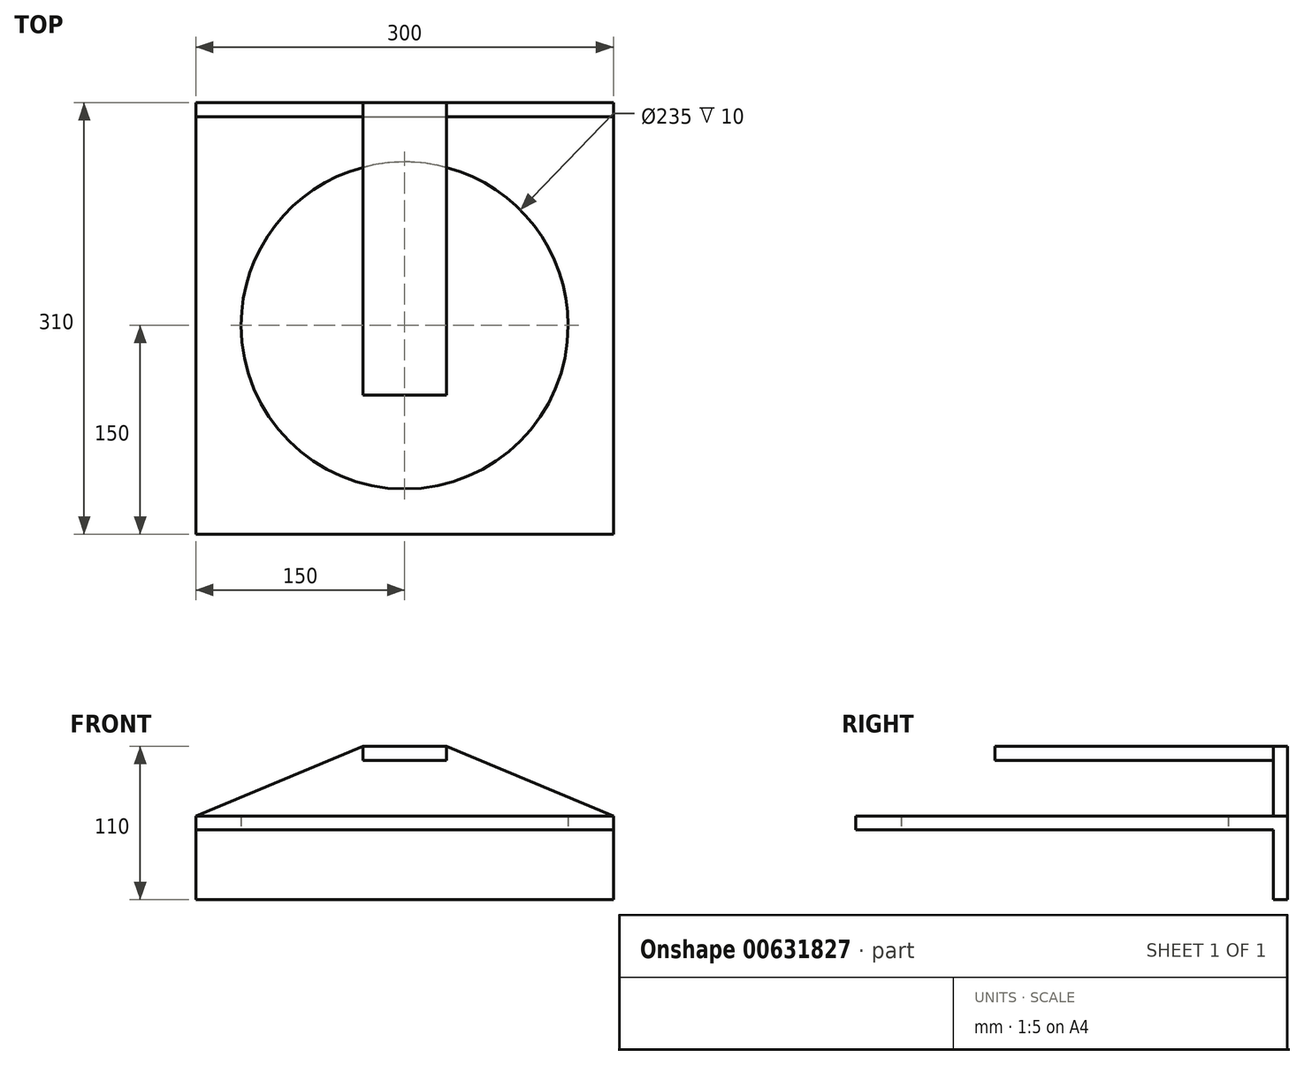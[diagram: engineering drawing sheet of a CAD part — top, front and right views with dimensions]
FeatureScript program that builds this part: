
annotation { "Feature Type Name" : "Feature", "Feature Type Description" : "" }
export const myFeature = defineFeature(function(context is Context, id is Id, definition is map)
    precondition{}
    {
        {
            var Q0;
            Q0=qCreatedBy(makeId("Front.planeOp"),FACE);
            var sketch = newSketch(context, id + "F0", { "sketchPlane" : qUnion([Q0])});
            skLineSegment(sketch, "E0.bottom", {"start": v(150, -30) * mm, "end": v(-150, -30) * mm});
            skLineSegment(sketch, "E0.top", {"start": v(150, 30) * mm, "end": v(-150, 30) * mm});
            skLineSegment(sketch, "E0.left", {"start": v(150, -30) * mm, "end": v(150, 30) * mm});
            skLineSegment(sketch, "E0.right", {"start": v(-150, -30) * mm, "end": v(-150, 30) * mm});
            skPoint(sketch, "E0.middle", {"position": v(0, 0) * mm});
            skLineSegment(sketch, "E1", {"start": v(0, 80) * mm, "end": v(-30, 80) * mm});
            skLineSegment(sketch, "E2", {"start": v(-30, 80) * mm, "end": v(-150, 30) * mm});
            skLineSegment(sketch, "E3", {"start": v(30, 80) * mm, "end": v(150, 30) * mm});
            skLineSegment(sketch, "E4", {"start": v(0, 80) * mm, "end": v(30, 80) * mm});
            skLineSegment(sketch, "E5", {"start": v(0, 80) * mm, "end": v(0, 30) * mm, "construction": true});
            skSolve(sketch);
        }
        {
            var Q0;
            Q0 = qSketchRegion(id + "F0", true);
            extrude(context, id + "F1", {"entities" : qUnion([Q0]), "depth" : 10 * mm, "offsetDistance" : 25 * mm});
        }
        {
            var Q0;
            Q0=makeQuery(id+"F1.opExtrude","CAP_FACE",FACE,{"disambiguationData":[OSD([sQuery(id+"F0.wireOp",EDGE,"E0.bottom"),sQuery(id+"F0.wireOp",EDGE,"E0.top"),sQuery(id+"F0.wireOp",EDGE,"E0.left"),sQuery(id+"F0.wireOp",EDGE,"E0.right")])],"isStart":false});
            var sketch = newSketch(context, id + "F2", { "sketchPlane" : qUnion([Q0])});
            skLineSegment(sketch, "E6.bottom", {"start": v(-150, 30) * mm, "end": v(150, 30) * mm});
            skLineSegment(sketch, "E6.top", {"start": v(-150, 20) * mm, "end": v(150, 20) * mm});
            skLineSegment(sketch, "E6.left", {"start": v(-150, 30) * mm, "end": v(-150, 20) * mm});
            skLineSegment(sketch, "E6.right", {"start": v(150, 30) * mm, "end": v(150, 20) * mm});
            skSolve(sketch);
        }
        {
            var Q0;
            Q0 = qSketchRegion(id + "F2", true);
            extrude(context, id + "F3", {"entities" : qUnion([Q0]), "operationType" : NewBodyOperationType.ADD, "depth" : 300 * mm, "offsetDistance" : 25 * mm});
        }
        {
            var Q0;
            Q0=makeQuery(id+"F3.opExtrude","SWEPT_FACE",FACE,{"disambiguationData":[OSD([sQuery(id+"F2.wireOp",EDGE,"E6.top")])]});
            var sketch = newSketch(context, id + "F4", { "sketchPlane" : qUnion([Q0])});
            skPoint(sketch, "E7", {"position": v(0, 160) * mm});
            skCircle(sketch, "E8", {"center": v(0, 160) * mm, "radius": 117.5 * mm});
            skSolve(sketch);
        }
        {
            var Q0;
            Q0=makeQuery(id+"F4.imprint","IMPRINT",FACE,{"disambiguationData":[TD([[makeQuery(id+"F4.imprint","IMPRINT",EDGE,{"derivedFrom":sQuery(id+"F4.wireOp",EDGE,"E8")}),1.0]])]});
            extrude(context, id + "F5", {"entities" : qUnion([Q0]), "operationType" : NewBodyOperationType.REMOVE, "endBound" : BoundingType.THROUGH_ALL, "oppositeDirection" : true, "depth" : 10 * mm, "offsetDistance" : 25 * mm});
        }
        {
            var Q0;
            {var subQ0=sQuery(id+"F0.wireOp",EDGE,"E2");var subQ1=sQuery(id+"F0.wireOp",EDGE,"E4");var subQ2=sQuery(id+"F0.wireOp",EDGE,"E1");var subQ3=sQuery(id+"F0.wireOp",EDGE,"E0.right");var subQ4=sQuery(id+"F0.wireOp",EDGE,"E0.left");var subQ5=sQuery(id+"F0.wireOp",EDGE,"E3");Q0=makeQuery(id+"F3.boolean.opBoolean","SPLIT",FACE,{"disambiguationData":[TD([makeQuery(id+"F1.opExtrude","SWEPT_FACE",FACE,{"disambiguationData":[OSD([subQ0])]})])],"derivedFrom":makeQuery(id+"F1.opExtrude","CAP_FACE",FACE,{"disambiguationData":[OSD([sQuery(id+"F0.wireOp",EDGE,"E0.bottom"),subQ4,subQ3,subQ2,subQ0,subQ5,subQ1])],"isStart":false})});}
            var sketch = newSketch(context, id + "F6", { "sketchPlane" : qUnion([Q0])});
            skLineSegment(sketch, "E9.bottom", {"start": v(-30, 80) * mm, "end": v(30, 80) * mm});
            skLineSegment(sketch, "E9.top", {"start": v(-30, 70) * mm, "end": v(30, 70) * mm});
            skLineSegment(sketch, "E9.left", {"start": v(-30, 80) * mm, "end": v(-30, 70) * mm});
            skLineSegment(sketch, "E9.right", {"start": v(30, 80) * mm, "end": v(30, 70) * mm});
            skSolve(sketch);
        }
        {
            var Q0;
            Q0 = qSketchRegion(id + "F6", true);
            extrude(context, id + "F7", {"entities" : qUnion([Q0]), "operationType" : NewBodyOperationType.ADD, "depth" : 200 * mm, "offsetDistance" : 25 * mm});
        }
    });
